# Revit family: Window-Wall_Unit_Quaker_R45F
name_source: partatom
category: Windows
units: mm (PartAtom-declared; Revit-internal decimal feet)

## family parameters
Always vertical = No
Cut with Voids When Loaded = No
Host = Wall
OmniClass Number = 23.30.20.00
OmniClass Title = Windows
Room Calculation Point = No
Shared = No

## types (66) — shared parameters
Analytic Construction = <None>
Default Sill Height = 36"
Define Thermal Properties by = Schematic Type
First Lite Unit = 36"
Keynote = 08 44 00
Manufacturer = Quaker Windows & Doors
Model = R45F
Product Page URL = https://www.arcat.com
Second Lite Unit = 60"
URL = https://www.quakerwindows.com
Wall Closure = By host
Window_FrameAwning_Viz = Yes
Window_FrameCasement_Viz = Yes
Window_FrameStandard_Viz = Yes
Window_Frame_Mat = Aluminum
Window_Glass_1Bay_Viz = Yes
Window_Glass_Mat = Glass
Window_Head_Viz = Yes
Window_Sill_ClipAnchor = Yes

## per-type parameters (varying)
- Single Lite Units - Left Jamb Unit: Awning Width=48 5/16"; Fixed Frame-1=Yes; Fixed Frame-2=Yes; Fixed Frame-3=Yes; Fourth Lite Unit=108"; Height=125 1/4"; Offset from Wall Center=0"; Rough Height=125 1/4"; Rough Width=59 23/32"; Third Lite Unit=84"; Width=59 23/32"; Window_Center Jabm_Viz=No; Window_CornerL_Viz=No; Window_CornerR_Viz=No; Window_Five Lite Mullion=No; Window_Four Lite Mullion=No; Window_Head_SlabClipGlass=No; Window_JambL&R_Viz=No; Window_JambL_Viz=No; Window_JambR_Viz=No; Window_Left Center Unit Casement=Yes; Window_Left Male & Female Corner=No; Window_Right Center Unit Casement=Yes; Window_Right Male & Female Corner_Viz=No; Window_Sill_04PSF_Viz=No; Window_Sill_12PSF_Viz=Yes; Window_Sill_15PSF_Viz=Yes; Window_Sill_SingleMullion=Yes; Window_Sill_SlabClip_Glass_Viz=No; Window_Sill_SlabClip_Metal_Viz=No; Window_Three Lite Mullion=Yes; Window_Two Lite Mullion=Yes; Wndow_Jamb Fixed-1=Yes
- Single Lite Units - Center Jamb Unit: Awning Width=60 19/32"; Fixed Frame-1=No; Fixed Frame-2=No; Fixed Frame-3=No; Fourth Lite Unit=126"; Height=150"; Offset from Wall Center=0"; Rough Height=150"; Rough Width=72"; Third Lite Unit=96"; Width=72"; Window_Center Jabm_Viz=Yes; Window_CornerL_Viz=No; Window_CornerR_Viz=No; Window_Five Lite Mullion=No; Window_Four Lite Mullion=No; Window_Head_SlabClipGlass=No; Window_JambL&R_Viz=No; Window_JambL_Viz=No; Window_JambR_Viz=No; Window_Left Center Unit Casement=No; Window_Left Male & Female Corner=No; Window_Right Center Unit Casement=No; Window_Right Male & Female Corner_Viz=No; Window_Sill_04PSF_Viz=No; Window_Sill_12PSF_Viz=No; Window_Sill_15PSF_Viz=Yes; Window_Sill_SingleMullion=Yes; Window_Sill_SlabClip_Glass_Viz=No; Window_Sill_SlabClip_Metal_Viz=No; Window_Three Lite Mullion=No; Window_Two Lite Mullion=No; Wndow_Jamb Fixed-1=No
- Single Lite Units - Right Jamb Unit: Awning Width=60 19/32"; Fixed Frame-1=No; Fixed Frame-2=No; Fixed Frame-3=No; Fourth Lite Unit=126"; Height=150"; Offset from Wall Center=0"; Rough Height=150"; Rough Width=72"; Third Lite Unit=96"; Width=72"; Window_Center Jabm_Viz=No; Window_CornerL_Viz=No; Window_CornerR_Viz=No; Window_Five Lite Mullion=No; Window_Four Lite Mullion=No; Window_Head_SlabClipGlass=No; Window_JambL&R_Viz=No; Window_JambL_Viz=No; Window_JambR_Viz=Yes; Window_Left Center Unit Casement=No; Window_Left Male & Female Corner=No; Window_Right Center Unit Casement=No; Window_Right Male & Female Corner_Viz=No; Window_Sill_04PSF_Viz=No; Window_Sill_12PSF_Viz=No; Window_Sill_15PSF_Viz=Yes; Window_Sill_SingleMullion=Yes; Window_Sill_SlabClip_Glass_Viz=No; Window_Sill_SlabClip_Metal_Viz=Yes; Window_Three Lite Mullion=No; Window_Two Lite Mullion=No; Wndow_Jamb Fixed-1=No
- Single Lite Units - Right  Left Jamb Unit: Awning Width=43 19/32"; Fixed Frame-1=No; Fixed Frame-2=No; Fixed Frame-3=No; Fourth Lite Unit=126"; Height=125 1/4"; Offset from Wall Center=31/32"; Rough Height=125 1/4"; Rough Width=55"; Third Lite Unit=96"; Width=55"; Window_Center Jabm_Viz=No; Window_CornerL_Viz=No; Window_CornerR_Viz=No; Window_Five Lite Mullion=No; Window_Four Lite Mullion=No; Window_Head_SlabClipGlass=No; Window_JambL&R_Viz=No; Window_JambL_Viz=Yes; Window_JambR_Viz=Yes; Window_Left Center Unit Casement=No; Window_Left Male & Female Corner=No; Window_Right Center Unit Casement=No; Window_Right Male & Female Corner_Viz=No; Window_Sill_04PSF_Viz=No; Window_Sill_12PSF_Viz=Yes; Window_Sill_15PSF_Viz=No; Window_Sill_SingleMullion=No; Window_Sill_SlabClip_Glass_Viz=No; Window_Sill_SlabClip_Metal_Viz=No; Window_Three Lite Mullion=No; Window_Two Lite Mullion=No; Wndow_Jamb Fixed-1=No
- Double Lite Units - No Vents In Top Lite of WW Unit - Left Jamb Unit: Awning Width=60 19/32"; Fixed Frame-1=No; Fixed Frame-2=No; Fixed Frame-3=No; Fourth Lite Unit=126"; Height=150"; Offset from Wall Center=0"; Rough Height=150"; Rough Width=72"; Third Lite Unit=96"; Width=72"; Window_Center Jabm_Viz=No; Window_CornerL_Viz=No; Window_CornerR_Viz=No; Window_Five Lite Mullion=No; Window_Four Lite Mullion=No; Window_Head_SlabClipGlass=No; Window_JambL&R_Viz=No; Window_JambL_Viz=Yes; Window_JambR_Viz=No; Window_Left Center Unit Casement=No; Window_Left Male & Female Corner=No; Window_Right Center Unit Casement=No; Window_Right Male & Female Corner_Viz=No; Window_Sill_04PSF_Viz=No; Window_Sill_12PSF_Viz=No; Window_Sill_15PSF_Viz=Yes; Window_Sill_SingleMullion=Yes; Window_Sill_SlabClip_Glass_Viz=No; Window_Sill_SlabClip_Metal_Viz=Yes; Window_Three Lite Mullion=No; Window_Two Lite Mullion=Yes; Wndow_Jamb Fixed-1=No
- Double Lite Units - No Vents In Top Lite of WW Unit - Center Jamb Unit: Awning Width=48 19/32"; Fixed Frame-1=No; Fixed Frame-2=No; Fixed Frame-3=No; Fourth Lite Unit=108"; Height=125 1/4"; Offset from Wall Center=0"; Rough Height=125 1/4"; Rough Width=60"; Third Lite Unit=84"; Width=60"; Window_Center Jabm_Viz=No; Window_CornerL_Viz=No; Window_CornerR_Viz=No; Window_Five Lite Mullion=No; Window_Four Lite Mullion=No; Window_Head_SlabClipGlass=No; Window_JambL&R_Viz=No; Window_JambL_Viz=No; Window_JambR_Viz=No; Window_Left Center Unit Casement=Yes; Window_Left Male & Female Corner=No; Window_Right Center Unit Casement=Yes; Window_Right Male & Female Corner_Viz=No; Window_Sill_04PSF_Viz=No; Window_Sill_12PSF_Viz=Yes; Window_Sill_15PSF_Viz=Yes; Window_Sill_SingleMullion=Yes; Window_Sill_SlabClip_Glass_Viz=No; Window_Sill_SlabClip_Metal_Viz=No; Window_Three Lite Mullion=No; Window_Two Lite Mullion=Yes; Wndow_Jamb Fixed-1=No
- Double Lite Units - No Vents In Top Lite of WW Unit - Right Jamb Unit: Awning Width=60 19/32"; Fixed Frame-1=No; Fixed Frame-2=No; Fixed Frame-3=No; Fourth Lite Unit=126"; Height=150"; Offset from Wall Center=0"; Rough Height=150"; Rough Width=72"; Third Lite Unit=96"; Width=72"; Window_Center Jabm_Viz=Yes; Window_CornerL_Viz=No; Window_CornerR_Viz=No; Window_Five Lite Mullion=No; Window_Four Lite Mullion=No; Window_Head_SlabClipGlass=No; Window_JambL&R_Viz=No; Window_JambL_Viz=No; Window_JambR_Viz=Yes; Window_Left Center Unit Casement=No; Window_Left Male & Female Corner=No; Window_Right Center Unit Casement=No; Window_Right Male & Female Corner_Viz=No; Window_Sill_04PSF_Viz=No; Window_Sill_12PSF_Viz=No; Window_Sill_15PSF_Viz=Yes; Window_Sill_SingleMullion=Yes; Window_Sill_SlabClip_Glass_Viz=No; Window_Sill_SlabClip_Metal_Viz=Yes; Window_Three Lite Mullion=No; Window_Two Lite Mullion=Yes; Wndow_Jamb Fixed-1=No
- Double Lite Units - No Vents In Top Lite of WW Unit - Right  Left Jamb Unit: Awning Width=60 19/32"; Fixed Frame-1=No; Fixed Frame-2=No; Fixed Frame-3=No; Fourth Lite Unit=126"; Height=150"; Offset from Wall Center=0"; Rough Height=150"; Rough Width=72"; Third Lite Unit=96"; Width=72"; Window_Center Jabm_Viz=Yes; Window_CornerL_Viz=No; Window_CornerR_Viz=No; Window_Five Lite Mullion=No; Window_Four Lite Mullion=No; Window_Head_SlabClipGlass=No; Window_JambL&R_Viz=Yes; Window_JambL_Viz=Yes; Window_JambR_Viz=Yes; Window_Left Center Unit Casement=No; Window_Left Male & Female Corner=No; Window_Right Center Unit Casement=No; Window_Right Male & Female Corner_Viz=No; Window_Sill_04PSF_Viz=No; Window_Sill_12PSF_Viz=No; Window_Sill_15PSF_Viz=Yes; Window_Sill_SingleMullion=Yes; Window_Sill_SlabClip_Glass_Viz=No; Window_Sill_SlabClip_Metal_Viz=Yes; Window_Three Lite Mullion=No; Window_Two Lite Mullion=Yes; Wndow_Jamb Fixed-1=No
- Triple Lite Units - No Vents In Top Lite of WW Unit - Left Jamb Unit: Awning Width=60 19/32"; Fixed Frame-1=No; Fixed Frame-2=No; Fixed Frame-3=No; Fourth Lite Unit=126"; Height=150"; Offset from Wall Center=0"; Rough Height=150"; Rough Width=72"; Third Lite Unit=96"; Width=72"; Window_Center Jabm_Viz=No; Window_CornerL_Viz=No; Window_CornerR_Viz=No; Window_Five Lite Mullion=No; Window_Four Lite Mullion=No; Window_Head_SlabClipGlass=No; Window_JambL&R_Viz=No; Window_JambL_Viz=Yes; Window_JambR_Viz=No; Window_Left Center Unit Casement=No; Window_Left Male & Female Corner=No; Window_Right Center Unit Casement=No; Window_Right Male & Female Corner_Viz=No; Window_Sill_04PSF_Viz=No; Window_Sill_12PSF_Viz=No; Window_Sill_15PSF_Viz=Yes; Window_Sill_SingleMullion=Yes; Window_Sill_SlabClip_Glass_Viz=No; Window_Sill_SlabClip_Metal_Viz=Yes; Window_Three Lite Mullion=Yes; Window_Two Lite Mullion=Yes; Wndow_Jamb Fixed-1=No
- Triple Lite Units - No Vents In Top Lite of WW Unit - Center Jamb Unit: Awning Width=24 19/32"; Fixed Frame-1=No; Fixed Frame-2=No; Fixed Frame-3=No; Fourth Lite Unit=108"; Height=125 1/4"; Offset from Wall Center=0"; Rough Height=125 1/4"; Rough Width=36"; Third Lite Unit=84"; Width=36"; Window_Center Jabm_Viz=No; Window_CornerL_Viz=No; Window_CornerR_Viz=No; Window_Five Lite Mullion=No; Window_Four Lite Mullion=No; Window_Head_SlabClipGlass=No; Window_JambL&R_Viz=No; Window_JambL_Viz=No; Window_JambR_Viz=No; Window_Left Center Unit Casement=Yes; Window_Left Male & Female Corner=No; Window_Right Center Unit Casement=Yes; Window_Right Male & Female Corner_Viz=No; Window_Sill_04PSF_Viz=No; Window_Sill_12PSF_Viz=Yes; Window_Sill_15PSF_Viz=Yes; Window_Sill_SingleMullion=Yes; Window_Sill_SlabClip_Glass_Viz=No; Window_Sill_SlabClip_Metal_Viz=No; Window_Three Lite Mullion=Yes; Window_Two Lite Mullion=Yes; Wndow_Jamb Fixed-1=No
- Triple Lite Units - No Vents In Top Lite of WW Unit - Right Jamb Unit: Awning Width=60 19/32"; Fixed Frame-1=No; Fixed Frame-2=No; Fixed Frame-3=No; Fourth Lite Unit=126"; Height=150"; Offset from Wall Center=0"; Rough Height=150"; Rough Width=72"; Third Lite Unit=96"; Width=72"; Window_Center Jabm_Viz=No; Window_CornerL_Viz=No; Window_CornerR_Viz=No; Window_Five Lite Mullion=No; Window_Four Lite Mullion=No; Window_Head_SlabClipGlass=No; Window_JambL&R_Viz=No; Window_JambL_Viz=No; Window_JambR_Viz=Yes; Window_Left Center Unit Casement=No; Window_Left Male & Female Corner=No; Window_Right Center Unit Casement=No; Window_Right Male & Female Corner_Viz=No; Window_Sill_04PSF_Viz=No; Window_Sill_12PSF_Viz=No; Window_Sill_15PSF_Viz=Yes; Window_Sill_SingleMullion=Yes; Window_Sill_SlabClip_Glass_Viz=No; Window_Sill_SlabClip_Metal_Viz=Yes; Window_Three Lite Mullion=Yes; Window_Two Lite Mullion=Yes; Wndow_Jamb Fixed-1=No
- Triple Lite Units - No Vents In Top Lite of WW Unit - Right  Left Jamb Unit: Awning Width=60 19/32"; Fixed Frame-1=No; Fixed Frame-2=No; Fixed Frame-3=No; Fourth Lite Unit=126"; Height=150"; Offset from Wall Center=0"; Rough Height=150"; Rough Width=72"; Third Lite Unit=96"; Width=72"; Window_Center Jabm_Viz=No; Window_CornerL_Viz=No; Window_CornerR_Viz=No; Window_Five Lite Mullion=No; Window_Four Lite Mullion=No; Window_Head_SlabClipGlass=No; Window_JambL&R_Viz=Yes; Window_JambL_Viz=No; Window_JambR_Viz=No; Window_Left Center Unit Casement=No; Window_Left Male & Female Corner=No; Window_Right Center Unit Casement=No; Window_Right Male & Female Corner_Viz=No; Window_Sill_04PSF_Viz=No; Window_Sill_12PSF_Viz=No; Window_Sill_15PSF_Viz=Yes; Window_Sill_SingleMullion=Yes; Window_Sill_SlabClip_Glass_Viz=No; Window_Sill_SlabClip_Metal_Viz=Yes; Window_Three Lite Mullion=Yes; Window_Two Lite Mullion=Yes; Wndow_Jamb Fixed-1=No
- Double Lite Units - No Vents In Top Lite of WW Unit - Center Jamb Unit at Male/Female Corner on Left Jamb: Awning Width=60 19/32"; Fixed Frame-1=No; Fixed Frame-2=No; Fixed Frame-3=No; Fourth Lite Unit=126"; Height=150"; Offset from Wall Center=0"; Rough Height=150"; Rough Width=72"; Third Lite Unit=96"; Width=72"; Window_Center Jabm_Viz=Yes; Window_CornerL_Viz=Yes; Window_CornerR_Viz=No; Window_Five Lite Mullion=No; Window_Four Lite Mullion=No; Window_Head_SlabClipGlass=No; Window_JambL&R_Viz=No; Window_JambL_Viz=No; Window_JambR_Viz=Yes; Window_Left Center Unit Casement=No; Window_Left Male & Female Corner=Yes; Window_Right Center Unit Casement=No; Window_Right Male & Female Corner_Viz=No; Window_Sill_04PSF_Viz=No; Window_Sill_12PSF_Viz=No; Window_Sill_15PSF_Viz=Yes; Window_Sill_SingleMullion=Yes; Window_Sill_SlabClip_Glass_Viz=No; Window_Sill_SlabClip_Metal_Viz=Yes; Window_Three Lite Mullion=No; Window_Two Lite Mullion=Yes; Wndow_Jamb Fixed-1=No
- Double Lite Units - No Vents In Top Lite of WW Unit - Center Jamb Unit at Male/Female Corner on Right Jamb: Awning Width=60 19/32"; Fixed Frame-1=No; Fixed Frame-2=No; Fixed Frame-3=No; Fourth Lite Unit=126"; Height=150"; Offset from Wall Center=0"; Rough Height=150"; Rough Width=72"; Third Lite Unit=96"; Width=72"; Window_Center Jabm_Viz=Yes; Window_CornerL_Viz=No; Window_CornerR_Viz=Yes; Window_Five Lite Mullion=No; Window_Four Lite Mullion=No; Window_Head_SlabClipGlass=No; Window_JambL&R_Viz=No; Window_JambL_Viz=No; Window_JambR_Viz=Yes; Window_Left Center Unit Casement=No; Window_Left Male & Female Corner=No; Window_Right Center Unit Casement=No; Window_Right Male & Female Corner_Viz=Yes; Window_Sill_04PSF_Viz=No; Window_Sill_12PSF_Viz=No; Window_Sill_15PSF_Viz=Yes; Window_Sill_SingleMullion=Yes; Window_Sill_SlabClip_Glass_Viz=No; Window_Sill_SlabClip_Metal_Viz=Yes; Window_Three Lite Mullion=No; Window_Two Lite Mullion=Yes; Wndow_Jamb Fixed-1=No
- Double Lite Units - No Vents In Top Lite of WW Unit - Right  Left Jamb Unit at Standard Corner on Left Jamb: Awning Width=60 19/32"; Fixed Frame-1=No; Fixed Frame-2=No; Fixed Frame-3=No; Fourth Lite Unit=126"; Height=150"; Offset from Wall Center=0"; Rough Height=150"; Rough Width=72"; Third Lite Unit=96"; Width=72"; Window_Center Jabm_Viz=Yes; Window_CornerL_Viz=Yes; Window_CornerR_Viz=No; Window_Five Lite Mullion=No; Window_Four Lite Mullion=No; Window_Head_SlabClipGlass=No; Window_JambL&R_Viz=Yes; Window_JambL_Viz=No; Window_JambR_Viz=Yes; Window_Left Center Unit Casement=No; Window_Left Male & Female Corner=No; Window_Right Center Unit Casement=No; Window_Right Male & Female Corner_Viz=No; Window_Sill_04PSF_Viz=No; Window_Sill_12PSF_Viz=No; Window_Sill_15PSF_Viz=Yes; Window_Sill_SingleMullion=Yes; Window_Sill_SlabClip_Glass_Viz=No; Window_Sill_SlabClip_Metal_Viz=Yes; Window_Three Lite Mullion=No; Window_Two Lite Mullion=Yes; Wndow_Jamb Fixed-1=No
- Double Lite Units - No Vents In Top Lite of WW Unit - Right  Left Jamb Unit at Standard Corner on Right Jamb: Awning Width=60 19/32"; Fixed Frame-1=No; Fixed Frame-2=No; Fixed Frame-3=No; Fourth Lite Unit=126"; Height=150"; Offset from Wall Center=0"; Rough Height=150"; Rough Width=72"; Third Lite Unit=96"; Width=72"; Window_Center Jabm_Viz=Yes; Window_CornerL_Viz=No; Window_CornerR_Viz=Yes; Window_Five Lite Mullion=No; Window_Four Lite Mullion=No; Window_Head_SlabClipGlass=No; Window_JambL&R_Viz=Yes; Window_JambL_Viz=No; Window_JambR_Viz=Yes; Window_Left Center Unit Casement=No; Window_Left Male & Female Corner=No; Window_Right Center Unit Casement=No; Window_Right Male & Female Corner_Viz=No; Window_Sill_04PSF_Viz=No; Window_Sill_12PSF_Viz=No; Window_Sill_15PSF_Viz=Yes; Window_Sill_SingleMullion=Yes; Window_Sill_SlabClip_Glass_Viz=No; Window_Sill_SlabClip_Metal_Viz=Yes; Window_Three Lite Mullion=No; Window_Two Lite Mullion=Yes; Wndow_Jamb Fixed-1=No
- Single Lite Units - Center Jamb Unit at Male/Female Corner on Left Jamb: Awning Width=60 19/32"; Fixed Frame-1=No; Fixed Frame-2=No; Fixed Frame-3=No; Fourth Lite Unit=126"; Height=150"; Offset from Wall Center=0"; Rough Height=150"; Rough Width=72"; Third Lite Unit=96"; Width=72"; Window_Center Jabm_Viz=Yes; Window_CornerL_Viz=No; Window_CornerR_Viz=No; Window_Five Lite Mullion=No; Window_Four Lite Mullion=No; Window_Head_SlabClipGlass=No; Window_JambL&R_Viz=No; Window_JambL_Viz=No; Window_JambR_Viz=Yes; Window_Left Center Unit Casement=No; Window_Left Male & Female Corner=Yes; Window_Right Center Unit Casement=No; Window_Right Male & Female Corner_Viz=No; Window_Sill_04PSF_Viz=No; Window_Sill_12PSF_Viz=No; Window_Sill_15PSF_Viz=Yes; Window_Sill_SingleMullion=Yes; Window_Sill_SlabClip_Glass_Viz=No; Window_Sill_SlabClip_Metal_Viz=Yes; Window_Three Lite Mullion=No; Window_Two Lite Mullion=No; Wndow_Jamb Fixed-1=No
- Single Lite Units - Center Jamb Unit at Male/Female Corner on Right Jamb: Awning Width=60 19/32"; Fixed Frame-1=No; Fixed Frame-2=No; Fixed Frame-3=No; Fourth Lite Unit=126"; Height=150"; Offset from Wall Center=0"; Rough Height=150"; Rough Width=72"; Third Lite Unit=96"; Width=72"; Window_Center Jabm_Viz=Yes; Window_CornerL_Viz=No; Window_CornerR_Viz=Yes; Window_Five Lite Mullion=No; Window_Four Lite Mullion=No; Window_Head_SlabClipGlass=No; Window_JambL&R_Viz=No; Window_JambL_Viz=No; Window_JambR_Viz=Yes; Window_Left Center Unit Casement=No; Window_Left Male & Female Corner=No; Window_Right Center Unit Casement=No; Window_Right Male & Female Corner_Viz=Yes; Window_Sill_04PSF_Viz=No; Window_Sill_12PSF_Viz=No; Window_Sill_15PSF_Viz=Yes; Window_Sill_SingleMullion=Yes; Window_Sill_SlabClip_Glass_Viz=No; Window_Sill_SlabClip_Metal_Viz=Yes; Window_Three Lite Mullion=No; Window_Two Lite Mullion=No; Wndow_Jamb Fixed-1=No
- Single Lite Units - Right  Left Jamb Unit at Standard Corner on Left Jamb: Awning Width=60 19/32"; Fixed Frame-1=No; Fixed Frame-2=No; Fixed Frame-3=No; Fourth Lite Unit=126"; Height=150"; Offset from Wall Center=0"; Rough Height=150"; Rough Width=72"; Third Lite Unit=96"; Width=72"; Window_Center Jabm_Viz=No; Window_CornerL_Viz=No; Window_CornerR_Viz=No; Window_Five Lite Mullion=No; Window_Four Lite Mullion=No; Window_Head_SlabClipGlass=No; Window_JambL&R_Viz=No; Window_JambL_Viz=No; Window_JambR_Viz=No; Window_Left Center Unit Casement=Yes; Window_Left Male & Female Corner=No; Window_Right Center Unit Casement=No; Window_Right Male & Female Corner_Viz=Yes; Window_Sill_04PSF_Viz=No; Window_Sill_12PSF_Viz=No; Window_Sill_15PSF_Viz=Yes; Window_Sill_SingleMullion=Yes; Window_Sill_SlabClip_Glass_Viz=No; Window_Sill_SlabClip_Metal_Viz=Yes; Window_Three Lite Mullion=No; Window_Two Lite Mullion=No; Wndow_Jamb Fixed-1=No
- Single Lite Units - Right  Left Jamb Unit at Standard Corner on Right Jamb: Awning Width=60 19/32"; Fixed Frame-1=No; Fixed Frame-2=No; Fixed Frame-3=No; Fourth Lite Unit=126"; Height=150"; Offset from Wall Center=0"; Rough Height=150"; Rough Width=72"; Third Lite Unit=96"; Width=72"; Window_Center Jabm_Viz=No; Window_CornerL_Viz=No; Window_CornerR_Viz=No; Window_Five Lite Mullion=No; Window_Four Lite Mullion=No; Window_Head_SlabClipGlass=No; Window_JambL&R_Viz=No; Window_JambL_Viz=No; Window_JambR_Viz=No; Window_Left Center Unit Casement=No; Window_Left Male & Female Corner=Yes; Window_Right Center Unit Casement=Yes; Window_Right Male & Female Corner_Viz=No; Window_Sill_04PSF_Viz=No; Window_Sill_12PSF_Viz=No; Window_Sill_15PSF_Viz=Yes; Window_Sill_SingleMullion=Yes; Window_Sill_SlabClip_Glass_Viz=No; Window_Sill_SlabClip_Metal_Viz=Yes; Window_Three Lite Mullion=No; Window_Two Lite Mullion=No; Wndow_Jamb Fixed-1=No
- Triple Lite Units - No Vents In Top Lite of WW Unit - Center Jamb Unit at Male/Female Corner on Left Jamb: Awning Width=60 19/32"; Fixed Frame-1=No; Fixed Frame-2=No; Fixed Frame-3=No; Fourth Lite Unit=126"; Height=150"; Offset from Wall Center=0"; Rough Height=150"; Rough Width=72"; Third Lite Unit=96"; Width=72"; Window_Center Jabm_Viz=Yes; Window_CornerL_Viz=No; Window_CornerR_Viz=No; Window_Five Lite Mullion=No; Window_Four Lite Mullion=No; Window_Head_SlabClipGlass=No; Window_JambL&R_Viz=No; Window_JambL_Viz=Yes; Window_JambR_Viz=No; Window_Left Center Unit Casement=No; Window_Left Male & Female Corner=Yes; Window_Right Center Unit Casement=No; Window_Right Male & Female Corner_Viz=No; Window_Sill_04PSF_Viz=No; Window_Sill_12PSF_Viz=No; Window_Sill_15PSF_Viz=Yes; Window_Sill_SingleMullion=Yes; Window_Sill_SlabClip_Glass_Viz=No; Window_Sill_SlabClip_Metal_Viz=Yes; Window_Three Lite Mullion=Yes; Window_Two Lite Mullion=Yes; Wndow_Jamb Fixed-1=No
- Triple Lite Units - No Vents In Top Lite of WW Unit - Center Jamb Unit at Male/Female Corner on Right Jamb: Awning Width=60 19/32"; Fixed Frame-1=No; Fixed Frame-2=No; Fixed Frame-3=No; Fourth Lite Unit=126"; Height=150"; Offset from Wall Center=0"; Rough Height=150"; Rough Width=72"; Third Lite Unit=96"; Width=72"; Window_Center Jabm_Viz=Yes; Window_CornerL_Viz=No; Window_CornerR_Viz=No; Window_Five Lite Mullion=No; Window_Four Lite Mullion=No; Window_Head_SlabClipGlass=No; Window_JambL&R_Viz=No; Window_JambL_Viz=Yes; Window_JambR_Viz=No; Window_Left Center Unit Casement=No; Window_Left Male & Female Corner=No; Window_Right Center Unit Casement=No; Window_Right Male & Female Corner_Viz=Yes; Window_Sill_04PSF_Viz=No; Window_Sill_12PSF_Viz=No; Window_Sill_15PSF_Viz=Yes; Window_Sill_SingleMullion=Yes; Window_Sill_SlabClip_Glass_Viz=No; Window_Sill_SlabClip_Metal_Viz=Yes; Window_Three Lite Mullion=Yes; Window_Two Lite Mullion=Yes; Wndow_Jamb Fixed-1=No
- Triple Lite Units - No Vents In Top Lite of WW Unit - Right  Left Jamb Unit at Standard Corner on Left Jamb: Awning Width=60 19/32"; Fixed Frame-1=No; Fixed Frame-2=No; Fixed Frame-3=No; Fourth Lite Unit=126"; Height=150"; Offset from Wall Center=0"; Rough Height=150"; Rough Width=72"; Third Lite Unit=96"; Width=72"; Window_Center Jabm_Viz=Yes; Window_CornerL_Viz=Yes; Window_CornerR_Viz=No; Window_Five Lite Mullion=No; Window_Four Lite Mullion=No; Window_Head_SlabClipGlass=No; Window_JambL&R_Viz=Yes; Window_JambL_Viz=No; Window_JambR_Viz=No; Window_Left Center Unit Casement=No; Window_Left Male & Female Corner=No; Window_Right Center Unit Casement=No; Window_Right Male & Female Corner_Viz=No; Window_Sill_04PSF_Viz=No; Window_Sill_12PSF_Viz=No; Window_Sill_15PSF_Viz=Yes; Window_Sill_SingleMullion=Yes; Window_Sill_SlabClip_Glass_Viz=No; Window_Sill_SlabClip_Metal_Viz=Yes; Window_Three Lite Mullion=Yes; Window_Two Lite Mullion=Yes; Wndow_Jamb Fixed-1=No
- Triple Lite Units - No Vents In Top Lite of WW Unit - Right  Left Jamb Unit at Standard Corner on Right Jamb: Awning Width=60 19/32"; Fixed Frame-1=No; Fixed Frame-2=No; Fixed Frame-3=No; Fourth Lite Unit=126"; Height=150"; Offset from Wall Center=0"; Rough Height=150"; Rough Width=72"; Third Lite Unit=96"; Width=72"; Window_Center Jabm_Viz=Yes; Window_CornerL_Viz=No; Window_CornerR_Viz=Yes; Window_Five Lite Mullion=No; Window_Four Lite Mullion=No; Window_Head_SlabClipGlass=No; Window_JambL&R_Viz=Yes; Window_JambL_Viz=No; Window_JambR_Viz=No; Window_Left Center Unit Casement=No; Window_Left Male & Female Corner=No; Window_Right Center Unit Casement=No; Window_Right Male & Female Corner_Viz=No; Window_Sill_04PSF_Viz=No; Window_Sill_12PSF_Viz=No; Window_Sill_15PSF_Viz=Yes; Window_Sill_SingleMullion=Yes; Window_Sill_SlabClip_Glass_Viz=No; Window_Sill_SlabClip_Metal_Viz=Yes; Window_Three Lite Mullion=Yes; Window_Two Lite Mullion=Yes; Wndow_Jamb Fixed-1=No
- Four Lite Units - No Vents In Top Lite of WW Unit - Center Jamb Unit: Awning Width=60 19/32"; Fixed Frame-1=No; Fixed Frame-2=No; Fixed Frame-3=No; Fourth Lite Unit=126"; Height=150"; Offset from Wall Center=0"; Rough Height=150"; Rough Width=72"; Third Lite Unit=96"; Width=72"; Window_Center Jabm_Viz=Yes; Window_CornerL_Viz=No; Window_CornerR_Viz=No; Window_Five Lite Mullion=No; Window_Four Lite Mullion=Yes; Window_Head_SlabClipGlass=No; Window_JambL&R_Viz=No; Window_JambL_Viz=No; Window_JambR_Viz=No; Window_Left Center Unit Casement=No; Window_Left Male & Female Corner=No; Window_Right Center Unit Casement=No; Window_Right Male & Female Corner_Viz=No; Window_Sill_04PSF_Viz=No; Window_Sill_12PSF_Viz=No; Window_Sill_15PSF_Viz=Yes; Window_Sill_SingleMullion=Yes; Window_Sill_SlabClip_Glass_Viz=No; Window_Sill_SlabClip_Metal_Viz=Yes; Window_Three Lite Mullion=Yes; Window_Two Lite Mullion=Yes; Wndow_Jamb Fixed-1=No
- Four Lite Units - No Vents In Top Lite of WW Unit - Center Jamb Unit at Male/Female Corner on Left Jamb: Awning Width=60 19/32"; Fixed Frame-1=No; Fixed Frame-2=No; Fixed Frame-3=No; Fourth Lite Unit=126"; Height=150"; Offset from Wall Center=0"; Rough Height=150"; Rough Width=72"; Third Lite Unit=96"; Width=72"; Window_Center Jabm_Viz=Yes; Window_CornerL_Viz=No; Window_CornerR_Viz=No; Window_Five Lite Mullion=No; Window_Four Lite Mullion=Yes; Window_Head_SlabClipGlass=No; Window_JambL&R_Viz=No; Window_JambL_Viz=Yes; Window_JambR_Viz=No; Window_Left Center Unit Casement=No; Window_Left Male & Female Corner=Yes; Window_Right Center Unit Casement=No; Window_Right Male & Female Corner_Viz=No; Window_Sill_04PSF_Viz=No; Window_Sill_12PSF_Viz=No; Window_Sill_15PSF_Viz=Yes; Window_Sill_SingleMullion=Yes; Window_Sill_SlabClip_Glass_Viz=No; Window_Sill_SlabClip_Metal_Viz=Yes; Window_Three Lite Mullion=Yes; Window_Two Lite Mullion=Yes; Wndow_Jamb Fixed-1=No
- Four Lite Units - No Vents In Top Lite of WW Unit - Center Jamb Unit at Male/Female Corner on Right Jamb: Awning Width=60 19/32"; Fixed Frame-1=No; Fixed Frame-2=No; Fixed Frame-3=No; Fourth Lite Unit=126"; Height=150"; Offset from Wall Center=0"; Rough Height=150"; Rough Width=72"; Third Lite Unit=96"; Width=72"; Window_Center Jabm_Viz=Yes; Window_CornerL_Viz=No; Window_CornerR_Viz=No; Window_Five Lite Mullion=No; Window_Four Lite Mullion=Yes; Window_Head_SlabClipGlass=No; Window_JambL&R_Viz=No; Window_JambL_Viz=Yes; Window_JambR_Viz=No; Window_Left Center Unit Casement=No; Window_Left Male & Female Corner=No; Window_Right Center Unit Casement=No; Window_Right Male & Female Corner_Viz=Yes; Window_Sill_04PSF_Viz=No; Window_Sill_12PSF_Viz=No; Window_Sill_15PSF_Viz=Yes; Window_Sill_SingleMullion=Yes; Window_Sill_SlabClip_Glass_Viz=No; Window_Sill_SlabClip_Metal_Viz=Yes; Window_Three Lite Mullion=Yes; Window_Two Lite Mullion=Yes; Wndow_Jamb Fixed-1=No
- Four Lite Units - No Vents In Top Lite of WW Unit - Left Jamb Unit: Awning Width=60 19/32"; Fixed Frame-1=No; Fixed Frame-2=No; Fixed Frame-3=No; Fourth Lite Unit=126"; Height=150"; Offset from Wall Center=0"; Rough Height=150"; Rough Width=72"; Third Lite Unit=96"; Width=72"; Window_Center Jabm_Viz=No; Window_CornerL_Viz=No; Window_CornerR_Viz=No; Window_Five Lite Mullion=No; Window_Four Lite Mullion=Yes; Window_Head_SlabClipGlass=No; Window_JambL&R_Viz=No; Window_JambL_Viz=Yes; Window_JambR_Viz=No; Window_Left Center Unit Casement=No; Window_Left Male & Female Corner=No; Window_Right Center Unit Casement=No; Window_Right Male & Female Corner_Viz=No; Window_Sill_04PSF_Viz=No; Window_Sill_12PSF_Viz=No; Window_Sill_15PSF_Viz=Yes; Window_Sill_SingleMullion=Yes; Window_Sill_SlabClip_Glass_Viz=No; Window_Sill_SlabClip_Metal_Viz=Yes; Window_Three Lite Mullion=Yes; Window_Two Lite Mullion=Yes; Wndow_Jamb Fixed-1=No
- Four Lite Units - No Vents In Top Lite of WW Unit - Right  Left Jamb Unit: Awning Width=60 19/32"; Fixed Frame-1=No; Fixed Frame-2=No; Fixed Frame-3=No; Fourth Lite Unit=126"; Height=150"; Offset from Wall Center=0"; Rough Height=150"; Rough Width=72"; Third Lite Unit=96"; Width=72"; Window_Center Jabm_Viz=No; Window_CornerL_Viz=No; Window_CornerR_Viz=No; Window_Five Lite Mullion=No; Window_Four Lite Mullion=Yes; Window_Head_SlabClipGlass=No; Window_JambL&R_Viz=Yes; Window_JambL_Viz=No; Window_JambR_Viz=No; Window_Left Center Unit Casement=No; Window_Left Male & Female Corner=No; Window_Right Center Unit Casement=No; Window_Right Male & Female Corner_Viz=No; Window_Sill_04PSF_Viz=No; Window_Sill_12PSF_Viz=No; Window_Sill_15PSF_Viz=Yes; Window_Sill_SingleMullion=Yes; Window_Sill_SlabClip_Glass_Viz=No; Window_Sill_SlabClip_Metal_Viz=Yes; Window_Three Lite Mullion=Yes; Window_Two Lite Mullion=Yes; Wndow_Jamb Fixed-1=No
- Four Lite Units - No Vents In Top Lite of WW Unit - Right  Left Jamb Unit at Standard Corner on Left Jamb: Awning Width=60 19/32"; Fixed Frame-1=No; Fixed Frame-2=No; Fixed Frame-3=No; Fourth Lite Unit=126"; Height=150"; Offset from Wall Center=0"; Rough Height=150"; Rough Width=72"; Third Lite Unit=96"; Width=72"; Window_Center Jabm_Viz=Yes; Window_CornerL_Viz=Yes; Window_CornerR_Viz=No; Window_Five Lite Mullion=No; Window_Four Lite Mullion=Yes; Window_Head_SlabClipGlass=No; Window_JambL&R_Viz=Yes; Window_JambL_Viz=No; Window_JambR_Viz=No; Window_Left Center Unit Casement=No; Window_Left Male & Female Corner=No; Window_Right Center Unit Casement=No; Window_Right Male & Female Corner_Viz=No; Window_Sill_04PSF_Viz=No; Window_Sill_12PSF_Viz=No; Window_Sill_15PSF_Viz=Yes; Window_Sill_SingleMullion=Yes; Window_Sill_SlabClip_Glass_Viz=No; Window_Sill_SlabClip_Metal_Viz=Yes; Window_Three Lite Mullion=Yes; Window_Two Lite Mullion=Yes; Wndow_Jamb Fixed-1=No
- Four Lite Units - No Vents In Top Lite of WW Unit - Right  Left Jamb Unit at Standard Corner on Right Jamb: Awning Width=60 19/32"; Fixed Frame-1=No; Fixed Frame-2=No; Fixed Frame-3=No; Fourth Lite Unit=126"; Height=150"; Offset from Wall Center=0"; Rough Height=150"; Rough Width=72"; Third Lite Unit=96"; Width=72"; Window_Center Jabm_Viz=Yes; Window_CornerL_Viz=No; Window_CornerR_Viz=Yes; Window_Five Lite Mullion=No; Window_Four Lite Mullion=Yes; Window_Head_SlabClipGlass=No; Window_JambL&R_Viz=Yes; Window_JambL_Viz=No; Window_JambR_Viz=No; Window_Left Center Unit Casement=No; Window_Left Male & Female Corner=No; Window_Right Center Unit Casement=No; Window_Right Male & Female Corner_Viz=No; Window_Sill_04PSF_Viz=No; Window_Sill_12PSF_Viz=No; Window_Sill_15PSF_Viz=Yes; Window_Sill_SingleMullion=Yes; Window_Sill_SlabClip_Glass_Viz=No; Window_Sill_SlabClip_Metal_Viz=Yes; Window_Three Lite Mullion=Yes; Window_Two Lite Mullion=Yes; Wndow_Jamb Fixed-1=No
- Four Lite Units - No Vents In Top Lite of WW Unit - Right Jamb Unit: Awning Width=60 19/32"; Fixed Frame-1=No; Fixed Frame-2=No; Fixed Frame-3=No; Fourth Lite Unit=126"; Height=150"; Offset from Wall Center=0"; Rough Height=150"; Rough Width=72"; Third Lite Unit=96"; Width=72"; Window_Center Jabm_Viz=No; Window_CornerL_Viz=No; Window_CornerR_Viz=No; Window_Five Lite Mullion=No; Window_Four Lite Mullion=Yes; Window_Head_SlabClipGlass=No; Window_JambL&R_Viz=No; Window_JambL_Viz=No; Window_JambR_Viz=Yes; Window_Left Center Unit Casement=No; Window_Left Male & Female Corner=No; Window_Right Center Unit Casement=No; Window_Right Male & Female Corner_Viz=No; Window_Sill_04PSF_Viz=No; Window_Sill_12PSF_Viz=No; Window_Sill_15PSF_Viz=Yes; Window_Sill_SingleMullion=Yes; Window_Sill_SlabClip_Glass_Viz=No; Window_Sill_SlabClip_Metal_Viz=Yes; Window_Three Lite Mullion=Yes; Window_Two Lite Mullion=Yes; Wndow_Jamb Fixed-1=No
- Five Lite Units - No Vents In Top Lite of WW Unit - Center Jamb Unit: Awning Width=60 19/32"; Fixed Frame-1=No; Fixed Frame-2=No; Fixed Frame-3=No; Fourth Lite Unit=126"; Height=150"; Offset from Wall Center=0"; Rough Height=150"; Rough Width=72"; Third Lite Unit=96"; Width=72"; Window_Center Jabm_Viz=Yes; Window_CornerL_Viz=No; Window_CornerR_Viz=No; Window_Five Lite Mullion=Yes; Window_Four Lite Mullion=Yes; Window_Head_SlabClipGlass=No; Window_JambL&R_Viz=No; Window_JambL_Viz=No; Window_JambR_Viz=No; Window_Left Center Unit Casement=No; Window_Left Male & Female Corner=No; Window_Right Center Unit Casement=No; Window_Right Male & Female Corner_Viz=No; Window_Sill_04PSF_Viz=No; Window_Sill_12PSF_Viz=No; Window_Sill_15PSF_Viz=Yes; Window_Sill_SingleMullion=Yes; Window_Sill_SlabClip_Glass_Viz=No; Window_Sill_SlabClip_Metal_Viz=Yes; Window_Three Lite Mullion=Yes; Window_Two Lite Mullion=Yes; Wndow_Jamb Fixed-1=No
- Five Lite Units - No Vents In Top Lite of WW Unit - Center Jamb Unit at Male/Female Corner on Left Jamb: Awning Width=60 19/32"; Fixed Frame-1=No; Fixed Frame-2=No; Fixed Frame-3=No; Fourth Lite Unit=126"; Height=150"; Offset from Wall Center=0"; Rough Height=150"; Rough Width=72"; Third Lite Unit=96"; Width=72"; Window_Center Jabm_Viz=Yes; Window_CornerL_Viz=No; Window_CornerR_Viz=No; Window_Five Lite Mullion=Yes; Window_Four Lite Mullion=Yes; Window_Head_SlabClipGlass=No; Window_JambL&R_Viz=No; Window_JambL_Viz=Yes; Window_JambR_Viz=No; Window_Left Center Unit Casement=No; Window_Left Male & Female Corner=Yes; Window_Right Center Unit Casement=No; Window_Right Male & Female Corner_Viz=No; Window_Sill_04PSF_Viz=No; Window_Sill_12PSF_Viz=No; Window_Sill_15PSF_Viz=Yes; Window_Sill_SingleMullion=Yes; Window_Sill_SlabClip_Glass_Viz=No; Window_Sill_SlabClip_Metal_Viz=Yes; Window_Three Lite Mullion=Yes; Window_Two Lite Mullion=Yes; Wndow_Jamb Fixed-1=No
- Five Lite Units - No Vents In Top Lite of WW Unit - Center Jamb Unit at Male/Female Corner on Right Jamb: Awning Width=60 19/32"; Fixed Frame-1=No; Fixed Frame-2=No; Fixed Frame-3=No; Fourth Lite Unit=126"; Height=150"; Offset from Wall Center=0"; Rough Height=150"; Rough Width=72"; Third Lite Unit=96"; Width=72"; Window_Center Jabm_Viz=Yes; Window_CornerL_Viz=No; Window_CornerR_Viz=No; Window_Five Lite Mullion=Yes; Window_Four Lite Mullion=Yes; Window_Head_SlabClipGlass=No; Window_JambL&R_Viz=No; Window_JambL_Viz=Yes; Window_JambR_Viz=No; Window_Left Center Unit Casement=No; Window_Left Male & Female Corner=No; Window_Right Center Unit Casement=No; Window_Right Male & Female Corner_Viz=Yes; Window_Sill_04PSF_Viz=No; Window_Sill_12PSF_Viz=No; Window_Sill_15PSF_Viz=Yes; Window_Sill_SingleMullion=Yes; Window_Sill_SlabClip_Glass_Viz=No; Window_Sill_SlabClip_Metal_Viz=Yes; Window_Three Lite Mullion=Yes; Window_Two Lite Mullion=Yes; Wndow_Jamb Fixed-1=No
- Five Lite Units - No Vents In Top Lite of WW Unit - Left Jamb Unit: Awning Width=60 19/32"; Fixed Frame-1=No; Fixed Frame-2=No; Fixed Frame-3=No; Fourth Lite Unit=126"; Height=150"; Offset from Wall Center=0"; Rough Height=150"; Rough Width=72"; Third Lite Unit=96"; Width=72"; Window_Center Jabm_Viz=No; Window_CornerL_Viz=No; Window_CornerR_Viz=No; Window_Five Lite Mullion=Yes; Window_Four Lite Mullion=Yes; Window_Head_SlabClipGlass=No; Window_JambL&R_Viz=No; Window_JambL_Viz=Yes; Window_JambR_Viz=No; Window_Left Center Unit Casement=No; Window_Left Male & Female Corner=No; Window_Right Center Unit Casement=No; Window_Right Male & Female Corner_Viz=No; Window_Sill_04PSF_Viz=No; Window_Sill_12PSF_Viz=No; Window_Sill_15PSF_Viz=Yes; Window_Sill_SingleMullion=Yes; Window_Sill_SlabClip_Glass_Viz=No; Window_Sill_SlabClip_Metal_Viz=Yes; Window_Three Lite Mullion=Yes; Window_Two Lite Mullion=Yes; Wndow_Jamb Fixed-1=No
- Five Lite Units - No Vents In Top Lite of WW Unit - Right  Left Jamb Unit: Awning Width=60 19/32"; Fixed Frame-1=No; Fixed Frame-2=No; Fixed Frame-3=No; Fourth Lite Unit=126"; Height=150"; Offset from Wall Center=0"; Rough Height=150"; Rough Width=72"; Third Lite Unit=96"; Width=72"; Window_Center Jabm_Viz=No; Window_CornerL_Viz=No; Window_CornerR_Viz=No; Window_Five Lite Mullion=Yes; Window_Four Lite Mullion=Yes; Window_Head_SlabClipGlass=No; Window_JambL&R_Viz=Yes; Window_JambL_Viz=No; Window_JambR_Viz=No; Window_Left Center Unit Casement=No; Window_Left Male & Female Corner=No; Window_Right Center Unit Casement=No; Window_Right Male & Female Corner_Viz=No; Window_Sill_04PSF_Viz=No; Window_Sill_12PSF_Viz=No; Window_Sill_15PSF_Viz=Yes; Window_Sill_SingleMullion=Yes; Window_Sill_SlabClip_Glass_Viz=No; Window_Sill_SlabClip_Metal_Viz=Yes; Window_Three Lite Mullion=Yes; Window_Two Lite Mullion=Yes; Wndow_Jamb Fixed-1=No
- Five Lite Units - No Vents In Top Lite of WW Unit - Right  Left Jamb Unit at Standard Corner on Left Jamb: Awning Width=60 19/32"; Fixed Frame-1=No; Fixed Frame-2=No; Fixed Frame-3=No; Fourth Lite Unit=126"; Height=150"; Offset from Wall Center=0"; Rough Height=150"; Rough Width=72"; Third Lite Unit=96"; Width=72"; Window_Center Jabm_Viz=Yes; Window_CornerL_Viz=Yes; Window_CornerR_Viz=No; Window_Five Lite Mullion=Yes; Window_Four Lite Mullion=Yes; Window_Head_SlabClipGlass=No; Window_JambL&R_Viz=Yes; Window_JambL_Viz=No; Window_JambR_Viz=No; Window_Left Center Unit Casement=No; Window_Left Male & Female Corner=No; Window_Right Center Unit Casement=No; Window_Right Male & Female Corner_Viz=No; Window_Sill_04PSF_Viz=No; Window_Sill_12PSF_Viz=No; Window_Sill_15PSF_Viz=Yes; Window_Sill_SingleMullion=Yes; Window_Sill_SlabClip_Glass_Viz=No; Window_Sill_SlabClip_Metal_Viz=Yes; Window_Three Lite Mullion=Yes; Window_Two Lite Mullion=Yes; Wndow_Jamb Fixed-1=No
- Five Lite Units - No Vents In Top Lite of WW Unit - Right  Left Jamb Unit at Standard Corner on Right Jamb: Awning Width=60 19/32"; Fixed Frame-1=No; Fixed Frame-2=No; Fixed Frame-3=No; Fourth Lite Unit=126"; Height=150"; Offset from Wall Center=0"; Rough Height=150"; Rough Width=72"; Third Lite Unit=96"; Width=72"; Window_Center Jabm_Viz=Yes; Window_CornerL_Viz=No; Window_CornerR_Viz=Yes; Window_Five Lite Mullion=Yes; Window_Four Lite Mullion=Yes; Window_Head_SlabClipGlass=No; Window_JambL&R_Viz=Yes; Window_JambL_Viz=No; Window_JambR_Viz=No; Window_Left Center Unit Casement=No; Window_Left Male & Female Corner=No; Window_Right Center Unit Casement=No; Window_Right Male & Female Corner_Viz=No; Window_Sill_04PSF_Viz=No; Window_Sill_12PSF_Viz=No; Window_Sill_15PSF_Viz=Yes; Window_Sill_SingleMullion=Yes; Window_Sill_SlabClip_Glass_Viz=No; Window_Sill_SlabClip_Metal_Viz=Yes; Window_Three Lite Mullion=Yes; Window_Two Lite Mullion=Yes; Wndow_Jamb Fixed-1=No
- Five Lite Units - No Vents In Top Lite of WW Unit - Right Jamb Unit: Awning Width=60 19/32"; Fixed Frame-1=No; Fixed Frame-2=No; Fixed Frame-3=No; Fourth Lite Unit=126"; Height=150"; Offset from Wall Center=0"; Rough Height=150"; Rough Width=72"; Third Lite Unit=96"; Width=72"; Window_Center Jabm_Viz=No; Window_CornerL_Viz=No; Window_CornerR_Viz=No; Window_Five Lite Mullion=Yes; Window_Four Lite Mullion=Yes; Window_Head_SlabClipGlass=No; Window_JambL&R_Viz=No; Window_JambL_Viz=No; Window_JambR_Viz=Yes; Window_Left Center Unit Casement=No; Window_Left Male & Female Corner=No; Window_Right Center Unit Casement=No; Window_Right Male & Female Corner_Viz=No; Window_Sill_04PSF_Viz=No; Window_Sill_12PSF_Viz=No; Window_Sill_15PSF_Viz=Yes; Window_Sill_SingleMullion=Yes; Window_Sill_SlabClip_Glass_Viz=No; Window_Sill_SlabClip_Metal_Viz=Yes; Window_Three Lite Mullion=Yes; Window_Two Lite Mullion=Yes; Wndow_Jamb Fixed-1=No
- Type 25: Awning Width=60 19/32"; Fixed Frame-1=No; Fixed Frame-2=No; Fixed Frame-3=No; Fourth Lite Unit=126"; Height=150"; Offset from Wall Center=0"; Rough Height=150"; Rough Width=72"; Third Lite Unit=96"; Width=72"; Window_Center Jabm_Viz=Yes; Window_CornerL_Viz=Yes; Window_CornerR_Viz=Yes; Window_Five Lite Mullion=No; Window_Four Lite Mullion=No; Window_Head_SlabClipGlass=Yes; Window_JambL&R_Viz=Yes; Window_JambL_Viz=Yes; Window_JambR_Viz=Yes; Window_Left Center Unit Casement=No; Window_Left Male & Female Corner=Yes; Window_Right Center Unit Casement=No; Window_Right Male & Female Corner_Viz=Yes; Window_Sill_04PSF_Viz=Yes; Window_Sill_12PSF_Viz=Yes; Window_Sill_15PSF_Viz=Yes; Window_Sill_SingleMullion=Yes; Window_Sill_SlabClip_Glass_Viz=Yes; Window_Sill_SlabClip_Metal_Viz=Yes; Window_Three Lite Mullion=Yes; Window_Two Lite Mullion=Yes; Wndow_Jamb Fixed-1=No
- Double Lite Units - No Vents In Top Lite of WW Unit - Left Jamb Unit at Male/Female Corner on Right Jamb: Awning Width=60 19/32"; Fixed Frame-1=No; Fixed Frame-2=No; Fixed Frame-3=No; Fourth Lite Unit=126"; Height=150"; Offset from Wall Center=0"; Rough Height=150"; Rough Width=72"; Third Lite Unit=96"; Width=72"; Window_Center Jabm_Viz=No; Window_CornerL_Viz=No; Window_CornerR_Viz=No; Window_Five Lite Mullion=No; Window_Four Lite Mullion=No; Window_Head_SlabClipGlass=No; Window_JambL&R_Viz=No; Window_JambL_Viz=Yes; Window_JambR_Viz=No; Window_Left Center Unit Casement=No; Window_Left Male & Female Corner=No; Window_Right Center Unit Casement=No; Window_Right Male & Female Corner_Viz=No; Window_Sill_04PSF_Viz=No; Window_Sill_12PSF_Viz=No; Window_Sill_15PSF_Viz=Yes; Window_Sill_SingleMullion=Yes; Window_Sill_SlabClip_Glass_Viz=No; Window_Sill_SlabClip_Metal_Viz=Yes; Window_Three Lite Mullion=No; Window_Two Lite Mullion=Yes; Wndow_Jamb Fixed-1=No
- Double Lite Units - No Vents In Top Lite of WW Unit - Left Jamb Unit at Standard Corner on Left Jamb: Awning Width=60 19/32"; Fixed Frame-1=No; Fixed Frame-2=No; Fixed Frame-3=No; Fourth Lite Unit=126"; Height=150"; Offset from Wall Center=0"; Rough Height=150"; Rough Width=72"; Third Lite Unit=96"; Width=72"; Window_Center Jabm_Viz=No; Window_CornerL_Viz=No; Window_CornerR_Viz=No; Window_Five Lite Mullion=No; Window_Four Lite Mullion=No; Window_Head_SlabClipGlass=No; Window_JambL&R_Viz=No; Window_JambL_Viz=Yes; Window_JambR_Viz=No; Window_Left Center Unit Casement=No; Window_Left Male & Female Corner=No; Window_Right Center Unit Casement=No; Window_Right Male & Female Corner_Viz=No; Window_Sill_04PSF_Viz=No; Window_Sill_12PSF_Viz=No; Window_Sill_15PSF_Viz=Yes; Window_Sill_SingleMullion=Yes; Window_Sill_SlabClip_Glass_Viz=No; Window_Sill_SlabClip_Metal_Viz=Yes; Window_Three Lite Mullion=No; Window_Two Lite Mullion=Yes; Wndow_Jamb Fixed-1=No
- Double Lite Units - No Vents In Top Lite of WW Unit - Right Jamb Unit at Male/Female Corner on Left Jamb: Awning Width=60 19/32"; Fixed Frame-1=No; Fixed Frame-2=No; Fixed Frame-3=No; Fourth Lite Unit=126"; Height=150"; Offset from Wall Center=0"; Rough Height=150"; Rough Width=72"; Third Lite Unit=96"; Width=72"; Window_Center Jabm_Viz=Yes; Window_CornerL_Viz=No; Window_CornerR_Viz=No; Window_Five Lite Mullion=No; Window_Four Lite Mullion=No; Window_Head_SlabClipGlass=No; Window_JambL&R_Viz=No; Window_JambL_Viz=No; Window_JambR_Viz=Yes; Window_Left Center Unit Casement=No; Window_Left Male & Female Corner=No; Window_Right Center Unit Casement=No; Window_Right Male & Female Corner_Viz=No; Window_Sill_04PSF_Viz=No; Window_Sill_12PSF_Viz=No; Window_Sill_15PSF_Viz=Yes; Window_Sill_SingleMullion=Yes; Window_Sill_SlabClip_Glass_Viz=No; Window_Sill_SlabClip_Metal_Viz=Yes; Window_Three Lite Mullion=No; Window_Two Lite Mullion=Yes; Wndow_Jamb Fixed-1=No
- Double Lite Units - No Vents In Top Lite of WW Unit - Right Jamb Unit at Standard Corner on Right Jamb: Awning Width=60 19/32"; Fixed Frame-1=No; Fixed Frame-2=No; Fixed Frame-3=No; Fourth Lite Unit=126"; Height=150"; Offset from Wall Center=0"; Rough Height=150"; Rough Width=72"; Third Lite Unit=96"; Width=72"; Window_Center Jabm_Viz=Yes; Window_CornerL_Viz=No; Window_CornerR_Viz=No; Window_Five Lite Mullion=No; Window_Four Lite Mullion=No; Window_Head_SlabClipGlass=No; Window_JambL&R_Viz=No; Window_JambL_Viz=No; Window_JambR_Viz=Yes; Window_Left Center Unit Casement=No; Window_Left Male & Female Corner=No; Window_Right Center Unit Casement=No; Window_Right Male & Female Corner_Viz=No; Window_Sill_04PSF_Viz=No; Window_Sill_12PSF_Viz=No; Window_Sill_15PSF_Viz=Yes; Window_Sill_SingleMullion=Yes; Window_Sill_SlabClip_Glass_Viz=No; Window_Sill_SlabClip_Metal_Viz=Yes; Window_Three Lite Mullion=No; Window_Two Lite Mullion=Yes; Wndow_Jamb Fixed-1=No
- Five Lite Units - No Vents In Top Lite of WW Unit - Left Jamb Unit at Male/Female Corner on Right Jamb: Awning Width=60 19/32"; Fixed Frame-1=No; Fixed Frame-2=No; Fixed Frame-3=No; Fourth Lite Unit=126"; Height=150"; Offset from Wall Center=0"; Rough Height=150"; Rough Width=72"; Third Lite Unit=96"; Width=72"; Window_Center Jabm_Viz=No; Window_CornerL_Viz=No; Window_CornerR_Viz=No; Window_Five Lite Mullion=Yes; Window_Four Lite Mullion=Yes; Window_Head_SlabClipGlass=No; Window_JambL&R_Viz=No; Window_JambL_Viz=Yes; Window_JambR_Viz=No; Window_Left Center Unit Casement=No; Window_Left Male & Female Corner=No; Window_Right Center Unit Casement=No; Window_Right Male & Female Corner_Viz=No; Window_Sill_04PSF_Viz=No; Window_Sill_12PSF_Viz=No; Window_Sill_15PSF_Viz=Yes; Window_Sill_SingleMullion=Yes; Window_Sill_SlabClip_Glass_Viz=No; Window_Sill_SlabClip_Metal_Viz=Yes; Window_Three Lite Mullion=Yes; Window_Two Lite Mullion=Yes; Wndow_Jamb Fixed-1=No
- Five Lite Units - No Vents In Top Lite of WW Unit - Left Jamb Unit at Standard Corner on Left Jamb: Awning Width=60 19/32"; Fixed Frame-1=No; Fixed Frame-2=No; Fixed Frame-3=No; Fourth Lite Unit=126"; Height=150"; Offset from Wall Center=0"; Rough Height=150"; Rough Width=72"; Third Lite Unit=96"; Width=72"; Window_Center Jabm_Viz=No; Window_CornerL_Viz=No; Window_CornerR_Viz=No; Window_Five Lite Mullion=Yes; Window_Four Lite Mullion=Yes; Window_Head_SlabClipGlass=No; Window_JambL&R_Viz=No; Window_JambL_Viz=Yes; Window_JambR_Viz=No; Window_Left Center Unit Casement=No; Window_Left Male & Female Corner=No; Window_Right Center Unit Casement=No; Window_Right Male & Female Corner_Viz=No; Window_Sill_04PSF_Viz=No; Window_Sill_12PSF_Viz=No; Window_Sill_15PSF_Viz=Yes; Window_Sill_SingleMullion=Yes; Window_Sill_SlabClip_Glass_Viz=No; Window_Sill_SlabClip_Metal_Viz=Yes; Window_Three Lite Mullion=Yes; Window_Two Lite Mullion=Yes; Wndow_Jamb Fixed-1=No
- Five Lite Units - No Vents In Top Lite of WW Unit - Right Jamb Unit at Male/Female Corner on Left Jamb: Awning Width=60 19/32"; Fixed Frame-1=No; Fixed Frame-2=No; Fixed Frame-3=No; Fourth Lite Unit=126"; Height=150"; Offset from Wall Center=0"; Rough Height=150"; Rough Width=72"; Third Lite Unit=96"; Width=72"; Window_Center Jabm_Viz=No; Window_CornerL_Viz=No; Window_CornerR_Viz=No; Window_Five Lite Mullion=Yes; Window_Four Lite Mullion=Yes; Window_Head_SlabClipGlass=No; Window_JambL&R_Viz=No; Window_JambL_Viz=No; Window_JambR_Viz=Yes; Window_Left Center Unit Casement=No; Window_Left Male & Female Corner=No; Window_Right Center Unit Casement=No; Window_Right Male & Female Corner_Viz=No; Window_Sill_04PSF_Viz=No; Window_Sill_12PSF_Viz=No; Window_Sill_15PSF_Viz=Yes; Window_Sill_SingleMullion=Yes; Window_Sill_SlabClip_Glass_Viz=No; Window_Sill_SlabClip_Metal_Viz=Yes; Window_Three Lite Mullion=Yes; Window_Two Lite Mullion=Yes; Wndow_Jamb Fixed-1=No
- Five Lite Units - No Vents In Top Lite of WW Unit - Right Jamb Unit at Standard Corner on Right Jamb: Awning Width=60 19/32"; Fixed Frame-1=No; Fixed Frame-2=No; Fixed Frame-3=No; Fourth Lite Unit=126"; Height=150"; Offset from Wall Center=0"; Rough Height=150"; Rough Width=72"; Third Lite Unit=96"; Width=72"; Window_Center Jabm_Viz=No; Window_CornerL_Viz=No; Window_CornerR_Viz=No; Window_Five Lite Mullion=Yes; Window_Four Lite Mullion=Yes; Window_Head_SlabClipGlass=No; Window_JambL&R_Viz=No; Window_JambL_Viz=No; Window_JambR_Viz=Yes; Window_Left Center Unit Casement=No; Window_Left Male & Female Corner=No; Window_Right Center Unit Casement=No; Window_Right Male & Female Corner_Viz=No; Window_Sill_04PSF_Viz=No; Window_Sill_12PSF_Viz=No; Window_Sill_15PSF_Viz=Yes; Window_Sill_SingleMullion=Yes; Window_Sill_SlabClip_Glass_Viz=No; Window_Sill_SlabClip_Metal_Viz=Yes; Window_Three Lite Mullion=Yes; Window_Two Lite Mullion=Yes; Wndow_Jamb Fixed-1=No
- Four Lite Units - No Vents In Top Lite of WW Unit - Left Jamb Unit at Male/Female Corner on Right Jamb: Awning Width=60 19/32"; Fixed Frame-1=No; Fixed Frame-2=No; Fixed Frame-3=No; Fourth Lite Unit=126"; Height=150"; Offset from Wall Center=0"; Rough Height=150"; Rough Width=72"; Third Lite Unit=96"; Width=72"; Window_Center Jabm_Viz=No; Window_CornerL_Viz=No; Window_CornerR_Viz=No; Window_Five Lite Mullion=No; Window_Four Lite Mullion=Yes; Window_Head_SlabClipGlass=No; Window_JambL&R_Viz=No; Window_JambL_Viz=Yes; Window_JambR_Viz=No; Window_Left Center Unit Casement=No; Window_Left Male & Female Corner=No; Window_Right Center Unit Casement=No; Window_Right Male & Female Corner_Viz=No; Window_Sill_04PSF_Viz=No; Window_Sill_12PSF_Viz=No; Window_Sill_15PSF_Viz=Yes; Window_Sill_SingleMullion=Yes; Window_Sill_SlabClip_Glass_Viz=No; Window_Sill_SlabClip_Metal_Viz=Yes; Window_Three Lite Mullion=Yes; Window_Two Lite Mullion=Yes; Wndow_Jamb Fixed-1=No
- Four Lite Units - No Vents In Top Lite of WW Unit - Left Jamb Unit at Standard Corner on Left Jamb: Awning Width=60 19/32"; Fixed Frame-1=No; Fixed Frame-2=No; Fixed Frame-3=No; Fourth Lite Unit=126"; Height=150"; Offset from Wall Center=0"; Rough Height=150"; Rough Width=72"; Third Lite Unit=96"; Width=72"; Window_Center Jabm_Viz=No; Window_CornerL_Viz=No; Window_CornerR_Viz=No; Window_Five Lite Mullion=No; Window_Four Lite Mullion=Yes; Window_Head_SlabClipGlass=No; Window_JambL&R_Viz=No; Window_JambL_Viz=Yes; Window_JambR_Viz=No; Window_Left Center Unit Casement=No; Window_Left Male & Female Corner=No; Window_Right Center Unit Casement=No; Window_Right Male & Female Corner_Viz=No; Window_Sill_04PSF_Viz=No; Window_Sill_12PSF_Viz=No; Window_Sill_15PSF_Viz=Yes; Window_Sill_SingleMullion=Yes; Window_Sill_SlabClip_Glass_Viz=No; Window_Sill_SlabClip_Metal_Viz=Yes; Window_Three Lite Mullion=Yes; Window_Two Lite Mullion=Yes; Wndow_Jamb Fixed-1=No
- Four Lite Units - No Vents In Top Lite of WW Unit - Right Jamb Unit at Male/Female Corner on Left Jamb: Awning Width=60 19/32"; Fixed Frame-1=No; Fixed Frame-2=No; Fixed Frame-3=No; Fourth Lite Unit=126"; Height=150"; Offset from Wall Center=0"; Rough Height=150"; Rough Width=72"; Third Lite Unit=96"; Width=72"; Window_Center Jabm_Viz=No; Window_CornerL_Viz=No; Window_CornerR_Viz=No; Window_Five Lite Mullion=No; Window_Four Lite Mullion=Yes; Window_Head_SlabClipGlass=No; Window_JambL&R_Viz=No; Window_JambL_Viz=No; Window_JambR_Viz=Yes; Window_Left Center Unit Casement=No; Window_Left Male & Female Corner=No; Window_Right Center Unit Casement=No; Window_Right Male & Female Corner_Viz=No; Window_Sill_04PSF_Viz=No; Window_Sill_12PSF_Viz=No; Window_Sill_15PSF_Viz=Yes; Window_Sill_SingleMullion=Yes; Window_Sill_SlabClip_Glass_Viz=No; Window_Sill_SlabClip_Metal_Viz=Yes; Window_Three Lite Mullion=Yes; Window_Two Lite Mullion=Yes; Wndow_Jamb Fixed-1=No
- Four Lite Units - No Vents In Top Lite of WW Unit - Right Jamb Unit at Standard Corner on Right Jamb: Awning Width=60 19/32"; Fixed Frame-1=No; Fixed Frame-2=No; Fixed Frame-3=No; Fourth Lite Unit=126"; Height=150"; Offset from Wall Center=0"; Rough Height=150"; Rough Width=72"; Third Lite Unit=96"; Width=72"; Window_Center Jabm_Viz=No; Window_CornerL_Viz=No; Window_CornerR_Viz=No; Window_Five Lite Mullion=No; Window_Four Lite Mullion=Yes; Window_Head_SlabClipGlass=No; Window_JambL&R_Viz=No; Window_JambL_Viz=No; Window_JambR_Viz=Yes; Window_Left Center Unit Casement=No; Window_Left Male & Female Corner=No; Window_Right Center Unit Casement=No; Window_Right Male & Female Corner_Viz=No; Window_Sill_04PSF_Viz=No; Window_Sill_12PSF_Viz=No; Window_Sill_15PSF_Viz=Yes; Window_Sill_SingleMullion=Yes; Window_Sill_SlabClip_Glass_Viz=No; Window_Sill_SlabClip_Metal_Viz=Yes; Window_Three Lite Mullion=Yes; Window_Two Lite Mullion=Yes; Wndow_Jamb Fixed-1=No
- Single Lite Units - Left Jamb Unit at Male/Female Corner on Right Jamb: Awning Width=24 19/32"; Fixed Frame-1=No; Fixed Frame-2=No; Fixed Frame-3=No; Fourth Lite Unit=108"; Height=125 1/4"; Offset from Wall Center=0"; Rough Height=125 1/4"; Rough Width=36"; Third Lite Unit=84"; Width=36"; Window_Center Jabm_Viz=Yes; Window_CornerL_Viz=No; Window_CornerR_Viz=No; Window_Five Lite Mullion=No; Window_Four Lite Mullion=No; Window_Head_SlabClipGlass=No; Window_JambL&R_Viz=No; Window_JambL_Viz=No; Window_JambR_Viz=No; Window_Left Center Unit Casement=No; Window_Left Male & Female Corner=No; Window_Right Center Unit Casement=No; Window_Right Male & Female Corner_Viz=No; Window_Sill_04PSF_Viz=No; Window_Sill_12PSF_Viz=No; Window_Sill_15PSF_Viz=Yes; Window_Sill_SingleMullion=Yes; Window_Sill_SlabClip_Glass_Viz=No; Window_Sill_SlabClip_Metal_Viz=No; Window_Three Lite Mullion=No; Window_Two Lite Mullion=No; Wndow_Jamb Fixed-1=No
- Single Lite Units - Left Jamb Unit at Standard Corner on Left Jamb: Awning Width=29 3/4"; Fixed Frame-1=No; Fixed Frame-2=No; Fixed Frame-3=No; Fourth Lite Unit=108"; Height=125 1/4"; Offset from Wall Center=0"; Rough Height=125 1/4"; Rough Width=41 5/32"; Third Lite Unit=84"; Width=41 5/32"; Window_Center Jabm_Viz=No; Window_CornerL_Viz=No; Window_CornerR_Viz=No; Window_Five Lite Mullion=No; Window_Four Lite Mullion=No; Window_Head_SlabClipGlass=No; Window_JambL&R_Viz=No; Window_JambL_Viz=No; Window_JambR_Viz=Yes; Window_Left Center Unit Casement=No; Window_Left Male & Female Corner=No; Window_Right Center Unit Casement=No; Window_Right Male & Female Corner_Viz=Yes; Window_Sill_04PSF_Viz=No; Window_Sill_12PSF_Viz=Yes; Window_Sill_15PSF_Viz=No; Window_Sill_SingleMullion=Yes; Window_Sill_SlabClip_Glass_Viz=No; Window_Sill_SlabClip_Metal_Viz=No; Window_Three Lite Mullion=No; Window_Two Lite Mullion=No; Wndow_Jamb Fixed-1=No
- Single Lite Units - Right Jamb Unit at Male/Female Corner on Left Jamb: Awning Width=60 19/32"; Fixed Frame-1=No; Fixed Frame-2=No; Fixed Frame-3=No; Fourth Lite Unit=126"; Height=150"; Offset from Wall Center=0"; Rough Height=150"; Rough Width=72"; Third Lite Unit=96"; Width=72"; Window_Center Jabm_Viz=No; Window_CornerL_Viz=No; Window_CornerR_Viz=No; Window_Five Lite Mullion=No; Window_Four Lite Mullion=No; Window_Head_SlabClipGlass=No; Window_JambL&R_Viz=No; Window_JambL_Viz=No; Window_JambR_Viz=Yes; Window_Left Center Unit Casement=No; Window_Left Male & Female Corner=No; Window_Right Center Unit Casement=No; Window_Right Male & Female Corner_Viz=No; Window_Sill_04PSF_Viz=No; Window_Sill_12PSF_Viz=No; Window_Sill_15PSF_Viz=Yes; Window_Sill_SingleMullion=Yes; Window_Sill_SlabClip_Glass_Viz=No; Window_Sill_SlabClip_Metal_Viz=Yes; Window_Three Lite Mullion=No; Window_Two Lite Mullion=No; Wndow_Jamb Fixed-1=No
- Single Lite Units - Right Jamb Unit at Standard Corner on Right Jamb: Awning Width=48 5/16"; Fixed Frame-1=No; Fixed Frame-2=No; Fixed Frame-3=No; Fourth Lite Unit=108"; Height=125 1/4"; Offset from Wall Center=0"; Rough Height=125 1/4"; Rough Width=59 23/32"; Third Lite Unit=84"; Width=59 23/32"; Window_Center Jabm_Viz=No; Window_CornerL_Viz=No; Window_CornerR_Viz=No; Window_Five Lite Mullion=No; Window_Four Lite Mullion=No; Window_Head_SlabClipGlass=No; Window_JambL&R_Viz=No; Window_JambL_Viz=Yes; Window_JambR_Viz=No; Window_Left Center Unit Casement=No; Window_Left Male & Female Corner=Yes; Window_Right Center Unit Casement=No; Window_Right Male & Female Corner_Viz=No; Window_Sill_04PSF_Viz=No; Window_Sill_12PSF_Viz=Yes; Window_Sill_15PSF_Viz=No; Window_Sill_SingleMullion=Yes; Window_Sill_SlabClip_Glass_Viz=No; Window_Sill_SlabClip_Metal_Viz=No; Window_Three Lite Mullion=No; Window_Two Lite Mullion=No; Wndow_Jamb Fixed-1=No
- Triple Lite Units - No Vents In Top Lite of WW Unit - Left Jamb Unit at Male/Female Corner on Right Jamb: Awning Width=60 19/32"; Fixed Frame-1=No; Fixed Frame-2=No; Fixed Frame-3=No; Fourth Lite Unit=126"; Height=150"; Offset from Wall Center=0"; Rough Height=150"; Rough Width=72"; Third Lite Unit=96"; Width=72"; Window_Center Jabm_Viz=No; Window_CornerL_Viz=No; Window_CornerR_Viz=No; Window_Five Lite Mullion=No; Window_Four Lite Mullion=No; Window_Head_SlabClipGlass=No; Window_JambL&R_Viz=No; Window_JambL_Viz=Yes; Window_JambR_Viz=No; Window_Left Center Unit Casement=No; Window_Left Male & Female Corner=No; Window_Right Center Unit Casement=No; Window_Right Male & Female Corner_Viz=No; Window_Sill_04PSF_Viz=No; Window_Sill_12PSF_Viz=No; Window_Sill_15PSF_Viz=Yes; Window_Sill_SingleMullion=Yes; Window_Sill_SlabClip_Glass_Viz=No; Window_Sill_SlabClip_Metal_Viz=Yes; Window_Three Lite Mullion=Yes; Window_Two Lite Mullion=Yes; Wndow_Jamb Fixed-1=No
- Triple Lite Units - No Vents In Top Lite of WW Unit - Left Jamb Unit at Standard Corner on Left Jamb: Awning Width=60 19/32"; Fixed Frame-1=No; Fixed Frame-2=No; Fixed Frame-3=No; Fourth Lite Unit=126"; Height=150"; Offset from Wall Center=0"; Rough Height=150"; Rough Width=72"; Third Lite Unit=96"; Width=72"; Window_Center Jabm_Viz=No; Window_CornerL_Viz=No; Window_CornerR_Viz=No; Window_Five Lite Mullion=No; Window_Four Lite Mullion=No; Window_Head_SlabClipGlass=No; Window_JambL&R_Viz=No; Window_JambL_Viz=Yes; Window_JambR_Viz=No; Window_Left Center Unit Casement=No; Window_Left Male & Female Corner=No; Window_Right Center Unit Casement=No; Window_Right Male & Female Corner_Viz=No; Window_Sill_04PSF_Viz=No; Window_Sill_12PSF_Viz=No; Window_Sill_15PSF_Viz=Yes; Window_Sill_SingleMullion=Yes; Window_Sill_SlabClip_Glass_Viz=No; Window_Sill_SlabClip_Metal_Viz=Yes; Window_Three Lite Mullion=Yes; Window_Two Lite Mullion=Yes; Wndow_Jamb Fixed-1=No
- Triple Lite Units - No Vents In Top Lite of WW Unit - Right Jamb Unit at Male/Female Corner on Left Jamb: Awning Width=60 19/32"; Fixed Frame-1=No; Fixed Frame-2=No; Fixed Frame-3=No; Fourth Lite Unit=126"; Height=150"; Offset from Wall Center=0"; Rough Height=150"; Rough Width=72"; Third Lite Unit=96"; Width=72"; Window_Center Jabm_Viz=No; Window_CornerL_Viz=No; Window_CornerR_Viz=No; Window_Five Lite Mullion=No; Window_Four Lite Mullion=No; Window_Head_SlabClipGlass=No; Window_JambL&R_Viz=No; Window_JambL_Viz=No; Window_JambR_Viz=Yes; Window_Left Center Unit Casement=No; Window_Left Male & Female Corner=No; Window_Right Center Unit Casement=No; Window_Right Male & Female Corner_Viz=No; Window_Sill_04PSF_Viz=No; Window_Sill_12PSF_Viz=No; Window_Sill_15PSF_Viz=Yes; Window_Sill_SingleMullion=Yes; Window_Sill_SlabClip_Glass_Viz=No; Window_Sill_SlabClip_Metal_Viz=Yes; Window_Three Lite Mullion=Yes; Window_Two Lite Mullion=Yes; Wndow_Jamb Fixed-1=No
- Triple Lite Units - No Vents In Top Lite of WW Unit - Right Jamb Unit at Standard Corner on Right Jamb: Awning Width=60 19/32"; Fixed Frame-1=No; Fixed Frame-2=No; Fixed Frame-3=No; Fourth Lite Unit=126"; Height=150"; Offset from Wall Center=0"; Rough Height=150"; Rough Width=72"; Third Lite Unit=96"; Width=72"; Window_Center Jabm_Viz=No; Window_CornerL_Viz=No; Window_CornerR_Viz=No; Window_Five Lite Mullion=No; Window_Four Lite Mullion=No; Window_Head_SlabClipGlass=No; Window_JambL&R_Viz=No; Window_JambL_Viz=No; Window_JambR_Viz=Yes; Window_Left Center Unit Casement=No; Window_Left Male & Female Corner=No; Window_Right Center Unit Casement=No; Window_Right Male & Female Corner_Viz=No; Window_Sill_04PSF_Viz=No; Window_Sill_12PSF_Viz=No; Window_Sill_15PSF_Viz=Yes; Window_Sill_SingleMullion=Yes; Window_Sill_SlabClip_Glass_Viz=No; Window_Sill_SlabClip_Metal_Viz=Yes; Window_Three Lite Mullion=Yes; Window_Two Lite Mullion=Yes; Wndow_Jamb Fixed-1=No
- Triple Lite Units - No Vents In Top Lite of WW Unit - Right Jamb Unit at Standard Corner: Awning Width=60 19/32"; Fixed Frame-1=No; Fixed Frame-2=No; Fixed Frame-3=No; Fourth Lite Unit=126"; Height=150"; Offset from Wall Center=0"; Rough Height=150"; Rough Width=72"; Third Lite Unit=96"; Width=72"; Window_Center Jabm_Viz=No; Window_CornerL_Viz=No; Window_CornerR_Viz=Yes; Window_Five Lite Mullion=No; Window_Four Lite Mullion=No; Window_Head_SlabClipGlass=No; Window_JambL&R_Viz=No; Window_JambL_Viz=No; Window_JambR_Viz=Yes; Window_Left Center Unit Casement=Yes; Window_Left Male & Female Corner=No; Window_Right Center Unit Casement=No; Window_Right Male & Female Corner_Viz=No; Window_Sill_04PSF_Viz=No; Window_Sill_12PSF_Viz=No; Window_Sill_15PSF_Viz=Yes; Window_Sill_SingleMullion=Yes; Window_Sill_SlabClip_Glass_Viz=No; Window_Sill_SlabClip_Metal_Viz=Yes; Window_Three Lite Mullion=Yes; Window_Two Lite Mullion=Yes; Wndow_Jamb Fixed-1=No
- Type 63: Awning Width=43 19/32"; Fixed Frame-1=No; Fixed Frame-2=No; Fixed Frame-3=No; Fourth Lite Unit=126"; Height=125 1/4"; Offset from Wall Center=1 3/8"; Rough Height=125 1/4"; Rough Width=55"; Third Lite Unit=96"; Width=55"; Window_Center Jabm_Viz=No; Window_CornerL_Viz=No; Window_CornerR_Viz=No; Window_Five Lite Mullion=No; Window_Four Lite Mullion=No; Window_Head_SlabClipGlass=No; Window_JambL&R_Viz=No; Window_JambL_Viz=Yes; Window_JambR_Viz=No; Window_Left Center Unit Casement=No; Window_Left Male & Female Corner=No; Window_Right Center Unit Casement=Yes; Window_Right Male & Female Corner_Viz=No; Window_Sill_04PSF_Viz=No; Window_Sill_12PSF_Viz=Yes; Window_Sill_15PSF_Viz=No; Window_Sill_SingleMullion=No; Window_Sill_SlabClip_Glass_Viz=No; Window_Sill_SlabClip_Metal_Viz=No; Window_Three Lite Mullion=No; Window_Two Lite Mullion=No; Wndow_Jamb Fixed-1=No
- Type 64: Awning Width=48 5/16"; Fixed Frame-1=Yes; Fixed Frame-2=Yes; Fixed Frame-3=Yes; Fourth Lite Unit=108"; Height=125 1/4"; Offset from Wall Center=0"; Rough Height=125 1/4"; Rough Width=59 23/32"; Third Lite Unit=84"; Width=59 23/32"; Window_Center Jabm_Viz=No; Window_CornerL_Viz=No; Window_CornerR_Viz=No; Window_Five Lite Mullion=No; Window_Four Lite Mullion=No; Window_Head_SlabClipGlass=No; Window_JambL&R_Viz=No; Window_JambL_Viz=No; Window_JambR_Viz=No; Window_Left Center Unit Casement=Yes; Window_Left Male & Female Corner=No; Window_Right Center Unit Casement=Yes; Window_Right Male & Female Corner_Viz=No; Window_Sill_04PSF_Viz=No; Window_Sill_12PSF_Viz=Yes; Window_Sill_15PSF_Viz=Yes; Window_Sill_SingleMullion=Yes; Window_Sill_SlabClip_Glass_Viz=No; Window_Sill_SlabClip_Metal_Viz=No; Window_Three Lite Mullion=Yes; Window_Two Lite Mullion=Yes; Wndow_Jamb Fixed-1=Yes
- Type 65: Awning Width=43 19/32"; Fixed Frame-1=No; Fixed Frame-2=No; Fixed Frame-3=No; Fourth Lite Unit=108"; Height=125 1/4"; Offset from Wall Center=1"; Rough Height=125 1/4"; Rough Width=55"; Third Lite Unit=84"; Width=55"; Window_Center Jabm_Viz=No; Window_CornerL_Viz=No; Window_CornerR_Viz=No; Window_Five Lite Mullion=No; Window_Four Lite Mullion=No; Window_Head_SlabClipGlass=No; Window_JambL&R_Viz=No; Window_JambL_Viz=No; Window_JambR_Viz=Yes; Window_Left Center Unit Casement=Yes; Window_Left Male & Female Corner=No; Window_Right Center Unit Casement=No; Window_Right Male & Female Corner_Viz=No; Window_Sill_04PSF_Viz=No; Window_Sill_12PSF_Viz=Yes; Window_Sill_15PSF_Viz=No; Window_Sill_SingleMullion=Yes; Window_Sill_SlabClip_Glass_Viz=No; Window_Sill_SlabClip_Metal_Viz=No; Window_Three Lite Mullion=No; Window_Two Lite Mullion=No; Wndow_Jamb Fixed-1=No
- Type 66: Awning Width=30 1/2"; Fixed Frame-1=No; Fixed Frame-2=No; Fixed Frame-3=No; Fourth Lite Unit=108"; Height=125 1/4"; Offset from Wall Center=0"; Rough Height=125 1/4"; Rough Width=41 29/32"; Third Lite Unit=84"; Width=41 29/32"; Window_Center Jabm_Viz=No; Window_CornerL_Viz=No; Window_CornerR_Viz=No; Window_Five Lite Mullion=No; Window_Four Lite Mullion=No; Window_Head_SlabClipGlass=No; Window_JambL&R_Viz=No; Window_JambL_Viz=No; Window_JambR_Viz=No; Window_Left Center Unit Casement=No; Window_Left Male & Female Corner=No; Window_Right Center Unit Casement=Yes; Window_Right Male & Female Corner_Viz=Yes; Window_Sill_04PSF_Viz=No; Window_Sill_12PSF_Viz=Yes; Window_Sill_15PSF_Viz=No; Window_Sill_SingleMullion=Yes; Window_Sill_SlabClip_Glass_Viz=No; Window_Sill_SlabClip_Metal_Viz=No; Window_Three Lite Mullion=No; Window_Two Lite Mullion=No; Wndow_Jamb Fixed-1=No

## geometry (parser evidence)
native form markers: Extrusion x1, Sweep x16
no freeform markers — native parametric forms only
